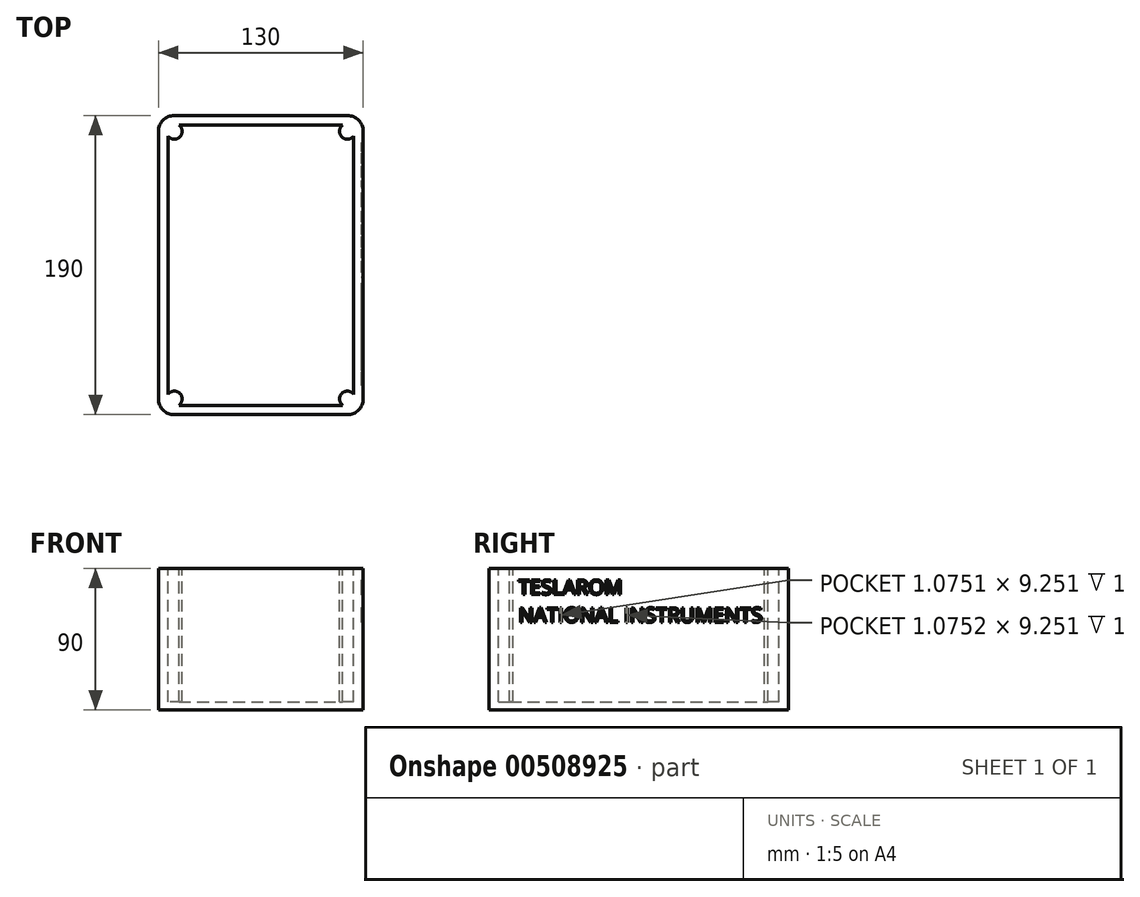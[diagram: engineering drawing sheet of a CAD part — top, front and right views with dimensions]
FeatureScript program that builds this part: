
annotation { "Feature Type Name" : "Feature", "Feature Type Description" : "" }
export const myFeature = defineFeature(function(context is Context, id is Id, definition is map)
    precondition{}
    {
        {
            var Q0;
            Q0=qCreatedBy(makeId("Top.planeOp"),FACE);
            var sketch = newSketch(context, id + "F0", { "sketchPlane" : qUnion([Q0])});
            skLineSegment(sketch, "E0.bottom", {"start": v(0, 0) * mm, "end": v(130, 0) * mm});
            skLineSegment(sketch, "E0.top", {"start": v(0, 190) * mm, "end": v(130, 190) * mm});
            skLineSegment(sketch, "E0.left", {"start": v(0, 0) * mm, "end": v(0, 190) * mm});
            skLineSegment(sketch, "E0.right", {"start": v(130, 0) * mm, "end": v(130, 190) * mm});
            skSolve(sketch);
        }
        {
            var Q0;
            Q0 = qSketchRegion(id + "F0", true);
            extrude(context, id + "F1", {"entities" : qUnion([Q0]), "depth" : 90 * mm});
        }
        {
            var Q0;
            Q0=makeQuery(id+"F1.opExtrude","SWEPT_EDGE",EDGE,{"disambiguationData":[OSD([sQuery(id+"F0.wireOp",EDGE,"E0.bottom"),sQuery(id+"F0.wireOp",EDGE,"E0.right")])]});
            var Q1;
            Q1=makeQuery(id+"F1.opExtrude","SWEPT_EDGE",EDGE,{"disambiguationData":[OSD([sQuery(id+"F0.wireOp",EDGE,"E0.top"),sQuery(id+"F0.wireOp",EDGE,"E0.right")])]});
            var Q2;
            Q2=makeQuery(id+"F1.opExtrude","SWEPT_EDGE",EDGE,{"disambiguationData":[OSD([sQuery(id+"F0.wireOp",EDGE,"E0.bottom"),sQuery(id+"F0.wireOp",EDGE,"E0.left")])]});
            var Q3;
            Q3=makeQuery(id+"F1.opExtrude","SWEPT_EDGE",EDGE,{"disambiguationData":[OSD([sQuery(id+"F0.wireOp",EDGE,"E0.top"),sQuery(id+"F0.wireOp",EDGE,"E0.left")])]});
            fillet(context, id + "F2", {"entities" : qUnion([Q0, Q1, Q2, Q3]), "radius" : 10 * mm, "tangentPropagation" : true, "allowEdgeOverflow" : false});
        }
        {
            var Q0;
            Q0=makeQuery(id+"F1.opExtrude","CAP_FACE",FACE,{"disambiguationData":[OSD([sQuery(id+"F0.wireOp",EDGE,"E0.bottom"),sQuery(id+"F0.wireOp",EDGE,"E0.top"),sQuery(id+"F0.wireOp",EDGE,"E0.left"),sQuery(id+"F0.wireOp",EDGE,"E0.right")])],"isStart":false});
            var sketch = newSketch(context, id + "F3", { "sketchPlane" : qUnion([Q0])});
            skLineSegment(sketch, "E1.0", {"start": v(13, 184) * mm, "end": v(117, 184) * mm});
            skLineSegment(sketch, "E2.0", {"start": v(124, 13) * mm, "end": v(124, 177) * mm});
            skLineSegment(sketch, "E3.0", {"start": v(6, 13) * mm, "end": v(6, 177) * mm});
            skLineSegment(sketch, "E4.0", {"start": v(13, 6) * mm, "end": v(117, 6) * mm});
            skArc(sketch, "E5", {"start": v(13, 6) * mm, "mid": v(13.54, 13.54) * mm, "end": v(6, 13) * mm});
            skArc(sketch, "E6", {"start": v(124, 13) * mm, "mid": v(116.46, 13.54) * mm, "end": v(117, 6) * mm});
            skArc(sketch, "E7", {"start": v(6, 177) * mm, "mid": v(13.54, 176.46) * mm, "end": v(13, 184) * mm});
            skArc(sketch, "E8", {"start": v(117, 184) * mm, "mid": v(116.46, 176.46) * mm, "end": v(124, 177) * mm});
            skSolve(sketch);
        }
        {
            var Q0;
            Q0 = qSketchRegion(id + "F3", true);
            extrude(context, id + "F4", {"entities" : qUnion([Q0]), "operationType" : NewBodyOperationType.REMOVE, "oppositeDirection" : true, "depth" : 85 * mm});
        }
        {
            var Q0;
            Q0=makeQuery(id+"F1.opExtrude","SWEPT_FACE",FACE,{"disambiguationData":[OSD([sQuery(id+"F0.wireOp",EDGE,"E0.right")])]});
            var sketch = newSketch(context, id + "F5", { "sketchPlane" : qUnion([Q0])});
            skText(sketch, "E9", { "text": "TESLAROM\nNATIONAL INSTRUMENTS", "fontName": "OpenSans-Regular.ttf"});
            const initialGuessF5  = {"E9": [0.01858, 0.0733, 1, 0, 0.00933]};
            skSetInitialGuess(sketch, initialGuessF5);
            skSolve(sketch);
        }
        {
            var Q0;
            Q0 = qSketchRegion(id + "F5", true);
            extrude(context, id + "F6", {"entities" : qUnion([Q0]), "operationType" : NewBodyOperationType.REMOVE, "oppositeDirection" : true, "depth" : 1 * mm});
        }
    });
